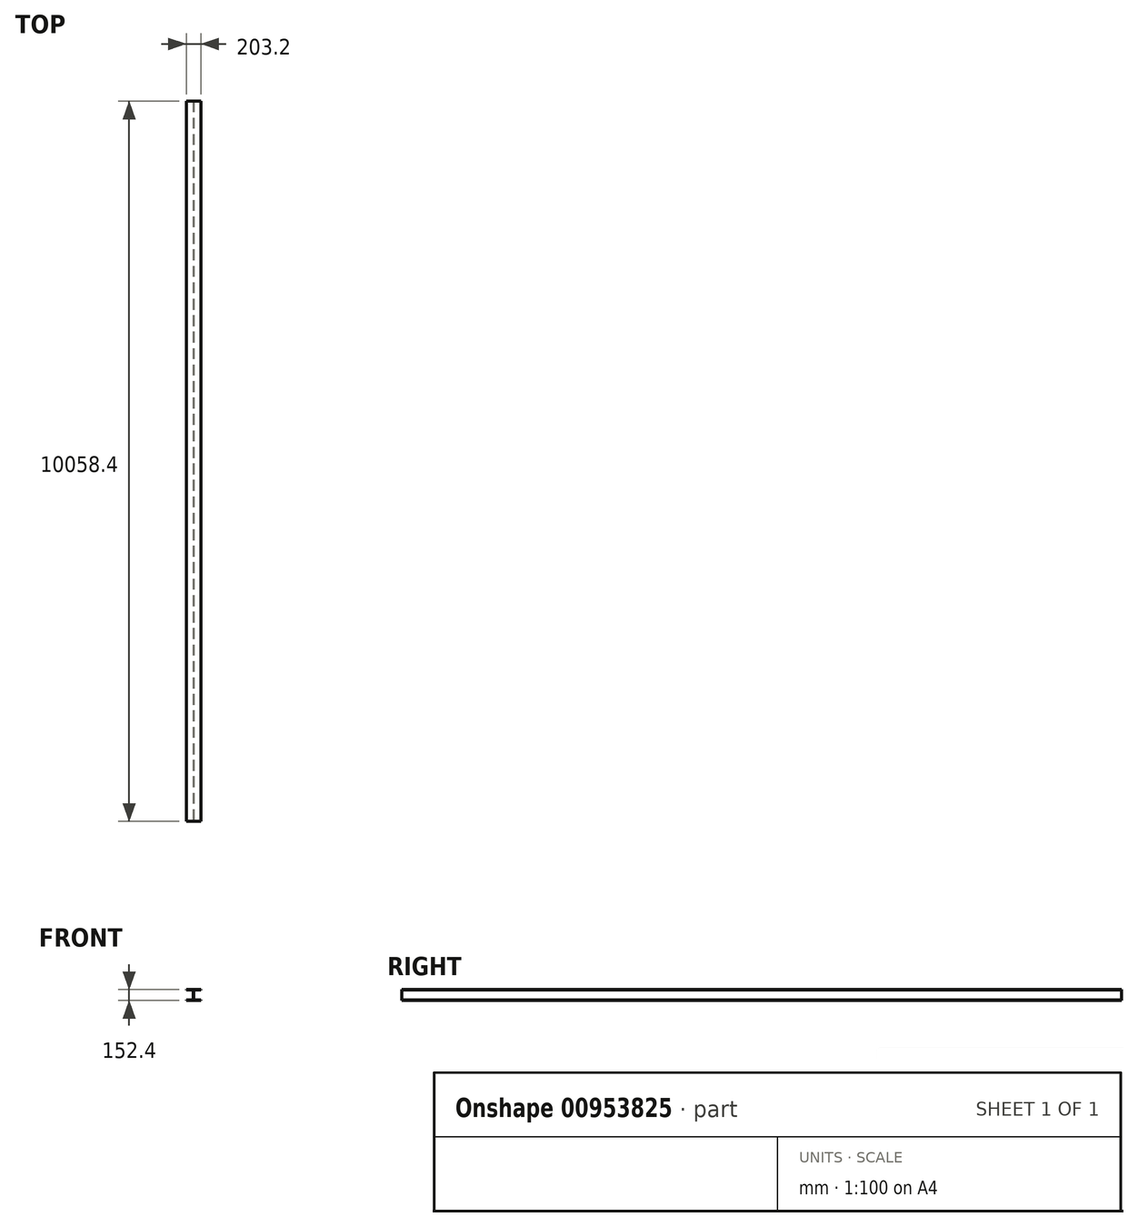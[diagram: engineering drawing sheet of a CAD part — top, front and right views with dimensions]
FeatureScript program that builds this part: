
annotation { "Feature Type Name" : "Feature", "Feature Type Description" : "" }
export const myFeature = defineFeature(function(context is Context, id is Id, definition is map)
    precondition{}
    {
        {
            var Q0;
            Q0=qCreatedBy(makeId("Front.planeOp"),FACE);
            var sketch = newSketch(context, id + "F0", { "sketchPlane" : qUnion([Q0])});
            skLineSegment(sketch, "E0.bottom", {"start": v(0, 0) * mm, "end": v(101.6, 0) * mm});
            skLineSegment(sketch, "E0.top", {"start": v(0, 152.4) * mm, "end": v(101.6, 152.4) * mm});
            skLineSegment(sketch, "E0.left", {"start": v(0, 0) * mm, "end": v(0, 152.4) * mm});
            skLineSegment(sketch, "E0.right", {"start": v(101.6, 0) * mm, "end": v(101.6, 6.35) * mm});
            skLineSegment(sketch, "E1.bottom", {"start": v(101.6, 6.35) * mm, "end": v(3.17, 6.35) * mm});
            skLineSegment(sketch, "E1.top", {"start": v(101.6, 146.05) * mm, "end": v(3.17, 146.05) * mm});
            skLineSegment(sketch, "E1.right", {"start": v(3.17, 6.35) * mm, "end": v(3.17, 146.05) * mm});
            skLineSegment(sketch, "E2.trimOffspring", {"start": v(101.6, 146.05) * mm, "end": v(101.6, 152.4) * mm});
            skSolve(sketch);
        }
        {
            var Q0;
            Q0 = qSketchRegion(id + "F0", true);
            extrude(context, id + "F1", {"entities" : qUnion([Q0]), "oppositeDirection" : true, "depth" : 10058.4 * mm, "offsetDistance" : 25.4 * mm});
        }
        {
            var Q0;
            Q0=makeQuery(id+"F1.opExtrude","SWEPT_BODY",BODY,{"disambiguationData":[OSD([sQuery(id+"F0.wireOp",EDGE,"E0.bottom"),sQuery(id+"F0.wireOp",EDGE,"E0.top"),sQuery(id+"F0.wireOp",EDGE,"E0.left"),sQuery(id+"F0.wireOp",EDGE,"E0.right"),sQuery(id+"F0.wireOp",EDGE,"E1.bottom"),sQuery(id+"F0.wireOp",EDGE,"E1.top"),sQuery(id+"F0.wireOp",EDGE,"E1.right"),sQuery(id+"F0.wireOp",EDGE,"E2.trimOffspring")])]});
            var Q1;
            Q1=makeQuery(id+"F1.opExtrude","SWEPT_FACE",FACE,{"disambiguationData":[OSD([sQuery(id+"F0.wireOp",EDGE,"E0.left")])]});
            mirror(context, id + "F2", {"operationType" : NewBodyOperationType.ADD, "entities" : qUnion([Q0]), "mirrorPlane" : qUnion([Q1])});
        }
    });
